# Revit family: Legrand_Lighting_Management_Standalone_Motion_Sensor_360D_Waterproof_White_Ceiling
name_source: partatom
category: Dispositifs d'éclairage
units: mm (PartAtom-declared; Revit-internal decimal feet)

## family parameters
Conserver l'orientation des annotations = Non
Cote de connecteur circulaire = Utiliser le diamètre
Couper avec des vides une fois chargée = Non
Hôte = Face
Partagée = Non
Point de calcul de pièce = Non
Type d'élément = Normal

## types (1)
- Legrand_Lighting_Management_Standalone_Motion_Sensor_360D_Waterproof_White_Ceiling
    Alarm function = no
    Code d'assemblage = D5010200
    Colour = White
    Constant light control = yes
    Degree of protection (IP) = IP55
    Description = PIR WATERPROOF MOTION SENSOR 360 DEGREES WHITE PLEXO
    Detection angle horizontal (MAX) (°) = 360
    Detection angle horizontal (MIN) (°) = 0
    Dim function with dimmer basic element = no
    ETIM-5.0 Class = EC000133
    Elévation par défaut = 0 mm  [stored 0 ft]
    Fabricant = LEGRAND
    Forced switch off = no
    Frequency (MAX) (Hz) = 60
    Frequency (MIN) (Hz) = 50
    General Conditions of Use = https://export.legrand.com
    HVAC-control = no
    Image du type = PH3.jpg
    Max. duty cycle (mn) = 16
    Max. starting current (A) = 8.5
    Max. switching power (W) = 1000
    Maximum mounting height (m) = 4
    Min. switch-on time (s) = 12
    Model = Movement sensor
    Mounting method = Surface mounted (plaster)
    Nominal voltage (V) = 230
    Product ID = 069780
    RAL-number (akin) = 9016
    Remote operation = no
    Response value luminosity (MAX) (lx) = 4000
    Response value luminosity (MIN) (lx) = 10
    Response value luminosity adjustable = yes
    Response value sensitivity adjustable = yes
    Substation input = no
    Suitable for wireless transmission = no
    Temperature (MAX) (°C) = 55
    Temperature (MIN) (°C) = 0
    URL = http://www.legrandoc.com
    Voltage type = AC

note: [stored X ft] marks values corroborated as IEEE doubles in the binary element streams (Revit-internal decimal feet)
